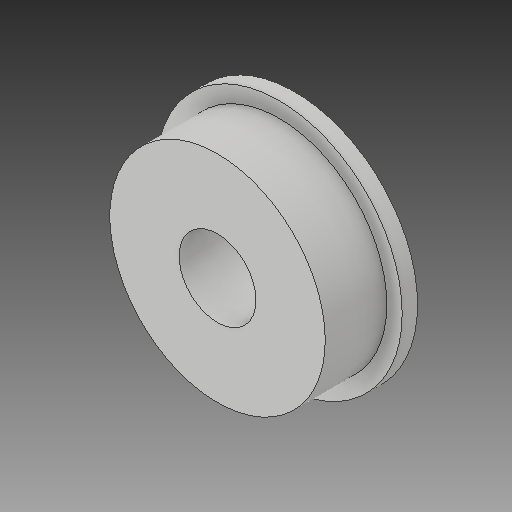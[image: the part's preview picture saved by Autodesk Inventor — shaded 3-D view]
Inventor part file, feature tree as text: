
AUTODESK INVENTOR PART (.ipt)
format: ipt  version: 2017 (Build 210142000, 142)  size: 129,536 bytes
history: native  units: mm
features: other x3, sketch x3
ambient origin geometry x8: Origin, YZ Plane, XZ Plane, XY Plane, X Axis, Y Axis, Z Axis, Center Point
bodies: Solid1 (feature_tree)
feature tree (6):
  other  "Flanged Bearing_CPY.ipt"
  other  "Solid1::Flanged Bearing_CPY.ipt"
  other  "TaggingFeature1"
  sketch  "Sketch1"  dims[d0=10.0mm]
  sketch  "Sketch2"
  sketch  "Sketch3"
